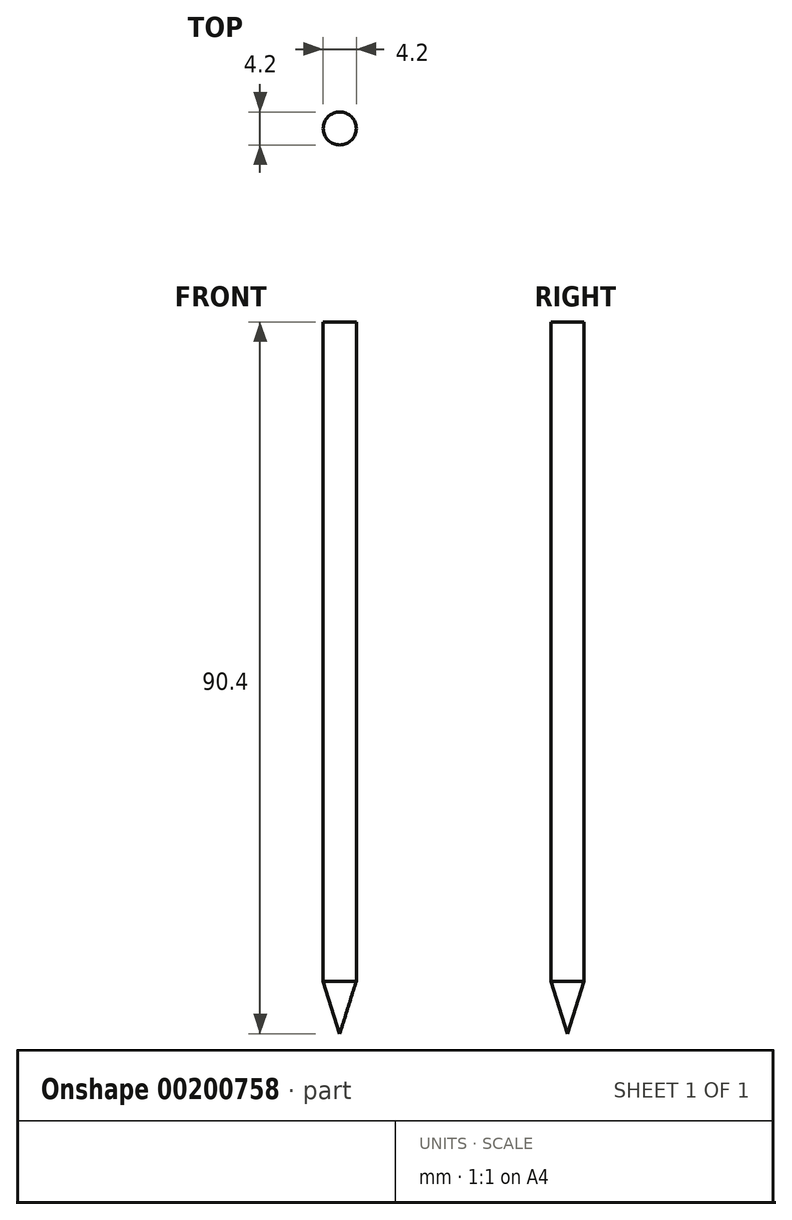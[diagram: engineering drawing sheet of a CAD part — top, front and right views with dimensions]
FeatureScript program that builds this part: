
annotation { "Feature Type Name" : "Feature", "Feature Type Description" : "" }
export const myFeature = defineFeature(function(context is Context, id is Id, definition is map)
    precondition{}
    {
        {
            var Q0;
            Q0=qCreatedBy(makeId("Front.planeOp"),FACE);
            var sketch = newSketch(context, id + "F0", { "sketchPlane" : qUnion([Q0])});
            skLineSegment(sketch, "E0", {"start": v(0, 31.57) * mm, "end": v(0, 31.57) * mm});
            skLineSegment(sketch, "E1", {"start": v(0, 31.57) * mm, "end": v(0, -39.2) * mm});
            skLineSegment(sketch, "E2", {"start": v(0, 31.57) * mm, "end": v(0, 51.21) * mm});
            skLineSegment(sketch, "E3", {"start": v(0, 51.21) * mm, "end": v(2.1, 51.21) * mm});
            skLineSegment(sketch, "E4", {"start": v(2.1, 51.21) * mm, "end": v(2.1, -32.52) * mm});
            skLineSegment(sketch, "E5", {"start": v(2.1, -32.52) * mm, "end": v(0, -39.2) * mm});
            skSolve(sketch);
        }
        {
            var Q0;
            Q0 = qSketchRegion(id + "F0", true);
            var Q1;
            Q1=sQuery(id+"F0.wireOp",EDGE,"E1");
            revolve(context, id + "F1", {"entities" : qUnion([Q0]), "axis" : qUnion([Q1]), "revolveType" : RevolveType.FULL});
        }
    });
